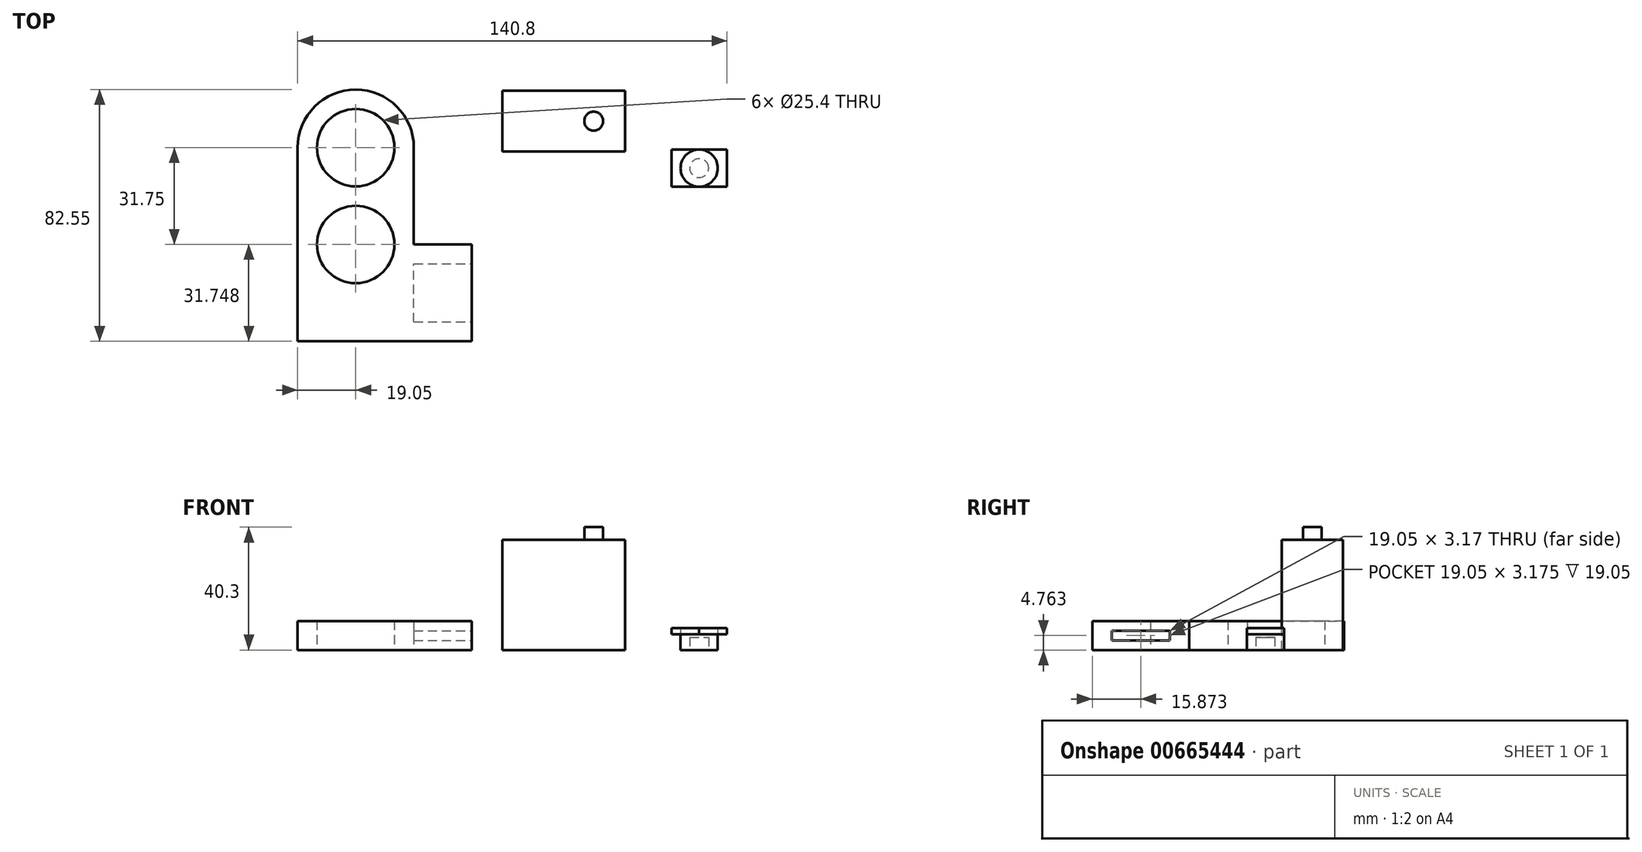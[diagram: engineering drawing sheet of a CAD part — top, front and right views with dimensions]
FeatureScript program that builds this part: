
annotation { "Feature Type Name" : "Feature", "Feature Type Description" : "" }
export const myFeature = defineFeature(function(context is Context, id is Id, definition is map)
    precondition{}
    {
        {
            var Q0;
            Q0=qCreatedBy(makeId("Front.planeOp"),FACE);
            var sketch = newSketch(context, id + "F0", { "sketchPlane" : qUnion([Q0])});
            skLineSegment(sketch, "E0.bottom", {"start": v(-19.76, 0) * mm, "end": v(20.54, 0) * mm});
            skLineSegment(sketch, "E0.top", {"start": v(-19.76, 36.1) * mm, "end": v(20.54, 36.1) * mm});
            skLineSegment(sketch, "E0.left", {"start": v(-19.76, 0) * mm, "end": v(-19.76, 36.1) * mm});
            skLineSegment(sketch, "E0.right", {"start": v(20.54, 0) * mm, "end": v(20.54, 36.1) * mm});
            skSolve(sketch);
        }
        {
            var Q0;
            Q0=makeQuery(id+"F0.imprint","IMPRINT",FACE,{"disambiguationData":[TD([[makeQuery(id+"F0.imprint","IMPRINT",EDGE,{"derivedFrom":sQuery(id+"F0.wireOp",EDGE,"E0.bottom")}),1.0]])]});
            extrude(context, id + "F1", {"entities" : qUnion([Q0]), "depth" : 20 * mm, "offsetDistance" : 25 * mm});
        }
        {
            var Q0;
            Q0=makeQuery(id+"F1.opExtrude","SWEPT_FACE",FACE,{"disambiguationData":[OSD([sQuery(id+"F0.wireOp",EDGE,"E0.top")])]});
            var sketch = newSketch(context, id + "F2", { "sketchPlane" : qUnion([Q0])});
            skCircle(sketch, "E1", {"center": v(10.24, -10) * mm, "radius": 3.1 * mm});
            skSolve(sketch);
        }
        {
            var Q0;
            Q0=makeQuery(id+"F2.imprint","IMPRINT",FACE,{"disambiguationData":[TD([[makeQuery(id+"F2.imprint","IMPRINT",EDGE,{"derivedFrom":sQuery(id+"F2.wireOp",EDGE,"E1")}),1.0]])]});
            extrude(context, id + "F3", {"entities" : qUnion([Q0]), "operationType" : NewBodyOperationType.ADD, "depth" : 4.2 * mm, "offsetDistance" : 25 * mm});
        }
        {
            var Q0;
            Q0=qCreatedBy(makeId("Top.planeOp"),FACE);
            var sketch = newSketch(context, id + "F4", { "sketchPlane" : qUnion([Q0])});
            skCircle(sketch, "E2", {"center": v(44.84, -25.4) * mm, "radius": 6.1 * mm});
            skSolve(sketch);
        }
        {
            var Q0;
            Q0=makeQuery(id+"F4.imprint","IMPRINT",FACE,{"disambiguationData":[TD([[makeQuery(id+"F4.imprint","IMPRINT",EDGE,{"derivedFrom":sQuery(id+"F4.wireOp",EDGE,"E2")}),1.0]])]});
            extrude(context, id + "F5", {"entities" : qUnion([Q0]), "depth" : 5.2 * mm, "offsetDistance" : 25 * mm});
        }
        {
            var Q0;
            Q0=makeQuery(id+"F5.opExtrude","CAP_FACE",FACE,{"disambiguationData":[OSD([sQuery(id+"F4.wireOp",EDGE,"E2")])],"isStart":true});
            var sketch = newSketch(context, id + "F6", { "sketchPlane" : qUnion([Q0])});
            skCircle(sketch, "E3", {"center": v(44.84, 25.4) * mm, "radius": 3.1 * mm});
            skSolve(sketch);
        }
        {
            var Q0;
            Q0=makeQuery(id+"F6.imprint","IMPRINT",FACE,{"disambiguationData":[TD([[makeQuery(id+"F6.imprint","IMPRINT",EDGE,{"derivedFrom":sQuery(id+"F6.wireOp",EDGE,"E3")}),1.0]])]});
            extrude(context, id + "F7", {"entities" : qUnion([Q0]), "operationType" : NewBodyOperationType.REMOVE, "oppositeDirection" : true, "depth" : 4.2 * mm, "offsetDistance" : 25 * mm});
        }
        {
            var Q0;
            Q0=makeQuery(id+"F5.opExtrude","CAP_FACE",FACE,{"disambiguationData":[OSD([sQuery(id+"F4.wireOp",EDGE,"E2")])],"isStart":false});
            var sketch = newSketch(context, id + "F8", { "sketchPlane" : qUnion([Q0])});
            skLineSegment(sketch, "E4.bottom", {"start": v(53.94, -19.3) * mm, "end": v(35.74, -19.3) * mm});
            skLineSegment(sketch, "E4.top", {"start": v(53.94, -31.5) * mm, "end": v(35.74, -31.5) * mm});
            skLineSegment(sketch, "E4.left", {"start": v(53.94, -19.3) * mm, "end": v(53.94, -31.5) * mm});
            skLineSegment(sketch, "E4.right", {"start": v(35.74, -19.3) * mm, "end": v(35.74, -31.5) * mm});
            skPoint(sketch, "E4.middle", {"position": v(44.84, -25.4) * mm});
            skSolve(sketch);
        }
        {
            var Q0;
            {var subQ0=sQuery(id+"F8.wireOp",EDGE,"E4.bottom");var subQ1=makeQuery(id+"F5.opExtrude","CAP_EDGE",EDGE,{"disambiguationData":[OSD([sQuery(id+"F4.wireOp",EDGE,"E2")])],"isStart":false});var subQ2=makeQuery(id+"F8.imprint","INTERSECT",VERTEX,{"disambiguationData":[OD(0.0)],"derivedFrom":[subQ1,subQ0]});Q0=makeQuery(id+"F8.imprint","IMPRINT",FACE,{"disambiguationData":[TD([[makeQuery(id+"F8.imprint","IMPRINT",EDGE,{"disambiguationData":[TD([[subQ2,-1.0]])],"derivedFrom":subQ0}),1.0]])]});}
            var Q1;
            {var subQ0=sQuery(id+"F8.wireOp",EDGE,"E4.right");Q1=makeQuery(id+"F8.imprint","IMPRINT",FACE,{"disambiguationData":[TD([[makeQuery(id+"F8.imprint","IMPRINT",EDGE,{"derivedFrom":subQ0}),1.0]])]});}
            var Q2;
            {var subQ0=sQuery(id+"F8.wireOp",EDGE,"E4.left");Q2=makeQuery(id+"F8.imprint","IMPRINT",FACE,{"disambiguationData":[TD([[makeQuery(id+"F8.imprint","IMPRINT",EDGE,{"derivedFrom":subQ0}),-1.0]])]});}
            extrude(context, id + "F9", {"entities" : qUnion([Q0, Q1, Q2]), "operationType" : NewBodyOperationType.ADD, "depth" : 2 * mm, "offsetDistance" : 25 * mm});
        }
        {
            var Q0;
            Q0=qCreatedBy(makeId("Top.planeOp"),FACE);
            var sketch = newSketch(context, id + "F10", { "sketchPlane" : qUnion([Q0])});
            skCircle(sketch, "E5", {"center": v(-67.81, -18.68) * mm, "radius": 19.05 * mm});
            skCircle(sketch, "E6", {"center": v(-67.81, -50.43) * mm, "radius": 19.05 * mm});
            skLineSegment(sketch, "E7.bottom", {"start": v(-55.11, -50.43) * mm, "end": v(-29.71, -50.43) * mm});
            skLineSegment(sketch, "E7.top", {"start": v(-55.11, -82.18) * mm, "end": v(-29.71, -82.18) * mm});
            skLineSegment(sketch, "E7.left", {"start": v(-55.11, -50.43) * mm, "end": v(-55.11, -82.18) * mm});
            skLineSegment(sketch, "E7.right", {"start": v(-29.71, -50.43) * mm, "end": v(-29.71, -82.18) * mm});
            skCircle(sketch, "E8.0", {"center": v(-67.81, -50.43) * mm, "radius": 12.7 * mm});
            skCircle(sketch, "E9.0", {"center": v(-67.81, -18.68) * mm, "radius": 12.7 * mm});
            skLineSegment(sketch, "E10", {"start": v(-86.86, -18.68) * mm, "end": v(-86.86, -50.43) * mm});
            skLineSegment(sketch, "E11", {"start": v(-48.76, -18.68) * mm, "end": v(-48.76, -50.43) * mm});
            skLineSegment(sketch, "E12", {"start": v(-86.86, -50.43) * mm, "end": v(-86.86, -82.18) * mm});
            skLineSegment(sketch, "E13", {"start": v(-86.86, -82.18) * mm, "end": v(-55.11, -82.18) * mm});
            skSolve(sketch);
        }
        {
            var Q0;
            {var subQ1=sQuery(id+"F10.wireOp",EDGE,"E7.top");Q0=makeQuery(id+"F10.imprint","IMPRINT",FACE,{"disambiguationData":[TD([[makeQuery(id+"F10.imprint","IMPRINT",EDGE,{"derivedFrom":subQ1}),1.0]])]});}
            var Q1;
            {var subQ0=sQuery(id+"F10.wireOp",EDGE,"E12");Q1=makeQuery(id+"F10.imprint","IMPRINT",FACE,{"disambiguationData":[TD([[makeQuery(id+"F10.imprint","IMPRINT",EDGE,{"derivedFrom":subQ0}),1.0]])]});}
            var Q2;
            {var subQ3=sQuery(id+"F10.wireOp",EDGE,"E6");var subQ6=sQuery(id+"F10.wireOp",EDGE,"E5");var subQ7=makeQuery(id+"F10.imprint","INTERSECT",VERTEX,{"disambiguationData":[OD(0.0)],"derivedFrom":[subQ6,subQ3]});Q2=makeQuery(id+"F10.imprint","IMPRINT",FACE,{"disambiguationData":[TD([[makeQuery(id+"F10.imprint","IMPRINT",EDGE,{"disambiguationData":[TD([[subQ7,-1.0]])],"derivedFrom":subQ6}),-1.0]])]});}
            var Q3;
            {var subQ0=sQuery(id+"F10.wireOp",EDGE,"E8.0");var subQ1=sQuery(id+"F10.wireOp",EDGE,"E5");var subQ2=makeQuery(id+"F10.imprint","INTERSECT",VERTEX,{"derivedFrom":[subQ1,subQ0]});Q3=makeQuery(id+"F10.imprint","IMPRINT",FACE,{"disambiguationData":[TD([[makeQuery(id+"F10.imprint","IMPRINT",EDGE,{"disambiguationData":[TD([[subQ2,-1.0]])],"derivedFrom":subQ1}),-1.0]])]});}
            var Q4;
            {var subQ1=sQuery(id+"F10.wireOp",EDGE,"E6");var subQ3=sQuery(id+"F10.wireOp",EDGE,"E7.left");var subQ4=makeQuery(id+"F10.imprint","INTERSECT",VERTEX,{"derivedFrom":[subQ1,subQ3]});Q4=makeQuery(id+"F10.imprint","IMPRINT",FACE,{"disambiguationData":[TD([[makeQuery(id+"F10.imprint","IMPRINT",EDGE,{"disambiguationData":[TD([[subQ4,-1.0]])],"derivedFrom":subQ1}),1.0]])]});}
            var Q5;
            {var subQ0=sQuery(id+"F10.wireOp",EDGE,"E10");Q5=makeQuery(id+"F10.imprint","IMPRINT",FACE,{"disambiguationData":[TD([[makeQuery(id+"F10.imprint","IMPRINT",EDGE,{"derivedFrom":subQ0}),1.0]])]});}
            var Q6;
            {var subQ0=sQuery(id+"F10.wireOp",EDGE,"E6");var subQ1=sQuery(id+"F10.wireOp",EDGE,"E5");var subQ2=makeQuery(id+"F10.imprint","INTERSECT",VERTEX,{"disambiguationData":[OD(0.0)],"derivedFrom":[subQ1,subQ0]});Q6=makeQuery(id+"F10.imprint","IMPRINT",FACE,{"disambiguationData":[TD([[makeQuery(id+"F10.imprint","IMPRINT",EDGE,{"disambiguationData":[TD([[subQ2,-1.0]])],"derivedFrom":subQ1}),1.0]])]});}
            var Q7;
            {var subQ0=sQuery(id+"F10.wireOp",EDGE,"E11");Q7=makeQuery(id+"F10.imprint","IMPRINT",FACE,{"disambiguationData":[TD([[makeQuery(id+"F10.imprint","IMPRINT",EDGE,{"derivedFrom":subQ0}),-1.0]])]});}
            var Q8;
            {var subQ6=sQuery(id+"F10.wireOp",EDGE,"E9.0");Q8=makeQuery(id+"F10.imprint","IMPRINT",FACE,{"disambiguationData":[TD([[makeQuery(id+"F10.imprint","IMPRINT",EDGE,{"derivedFrom":subQ6}),-1.0]])]});}
            extrude(context, id + "F11", {"entities" : qUnion([Q0, Q1, Q2, Q3, Q4, Q5, Q6, Q7, Q8]), "depth" : 9.52 * mm, "offsetDistance" : 25.4 * mm});
        }
        {
            var Q0;
            Q0=makeQuery(id+"F11.opExtrude","SWEPT_FACE",FACE,{"disambiguationData":[OSD([sQuery(id+"F10.wireOp",EDGE,"E7.right")])]});
            var sketch = newSketch(context, id + "F12", { "sketchPlane" : qUnion([Q0])});
            skLineSegment(sketch, "E14.bottom", {"start": v(-75.83, 6.35) * mm, "end": v(-56.78, 6.35) * mm});
            skLineSegment(sketch, "E14.top", {"start": v(-75.83, 3.18) * mm, "end": v(-56.78, 3.18) * mm});
            skLineSegment(sketch, "E14.left", {"start": v(-75.83, 6.35) * mm, "end": v(-75.83, 3.18) * mm});
            skLineSegment(sketch, "E14.right", {"start": v(-56.78, 6.35) * mm, "end": v(-56.78, 3.18) * mm});
            skSolve(sketch);
        }
        {
            var Q0;
            Q0=makeQuery(id+"F12.imprint","IMPRINT",FACE,{"disambiguationData":[TD([[makeQuery(id+"F12.imprint","IMPRINT",EDGE,{"derivedFrom":sQuery(id+"F12.wireOp",EDGE,"E14.bottom")}),-1.0]])]});
            extrude(context, id + "F13", {"entities" : qUnion([Q0]), "operationType" : NewBodyOperationType.REMOVE, "oppositeDirection" : true, "depth" : 19.05 * mm, "hasOffset" : true, "offsetDistance" : 25.4 * mm});
        }
    });
